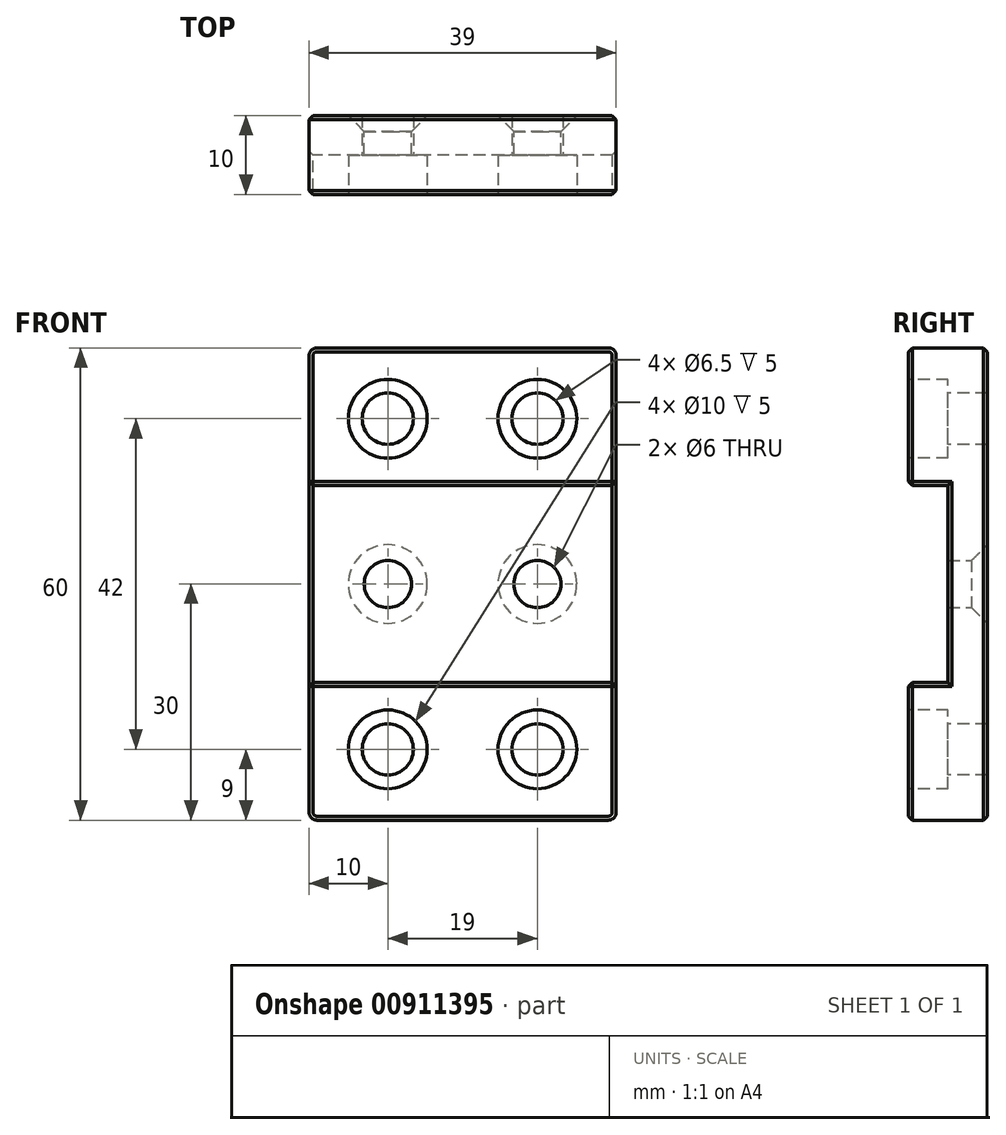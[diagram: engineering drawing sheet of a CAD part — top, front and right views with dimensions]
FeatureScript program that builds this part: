
annotation { "Feature Type Name" : "Feature", "Feature Type Description" : "" }
export const myFeature = defineFeature(function(context is Context, id is Id, definition is map)
    precondition{}
    {
        {
            var Q0;
            Q0=qCreatedBy(makeId("Right.planeOp"),FACE);
            var sketch = newSketch(context, id + "F0", { "sketchPlane" : qUnion([Q0])});
            skLineSegment(sketch, "E0", {"start": v(0, 0) * mm, "end": v(0, 60) * mm});
            skLineSegment(sketch, "E1", {"start": v(0, 60) * mm, "end": v(-10, 60) * mm});
            skLineSegment(sketch, "E2", {"start": v(-10, 60) * mm, "end": v(-10, 42.5) * mm});
            skLineSegment(sketch, "E3", {"start": v(-10, 42.5) * mm, "end": v(-5, 42.5) * mm});
            skLineSegment(sketch, "E4", {"start": v(-5, 42.5) * mm, "end": v(-5, 17.5) * mm});
            skLineSegment(sketch, "E5", {"start": v(-5, 17.5) * mm, "end": v(-10, 17.5) * mm});
            skLineSegment(sketch, "E6", {"start": v(-10, 17.5) * mm, "end": v(-10, 0) * mm});
            skLineSegment(sketch, "E7", {"start": v(-10, 0) * mm, "end": v(0, 0) * mm});
            skSolve(sketch);
        }
        {
            var Q0;
            Q0=makeQuery(id+"F0.imprint","IMPRINT",FACE,{"disambiguationData":[TD([[makeQuery(id+"F0.imprint","IMPRINT",EDGE,{"derivedFrom":sQuery(id+"F0.wireOp",EDGE,"E0")}),1.0]])]});
            extrude(context, id + "F1", {"entities" : qUnion([Q0]), "depth" : 39 * mm, "offsetDistance" : 25 * mm});
        }
        {
            var Q0;
            Q0=makeQuery(id+"F1.opExtrude","SWEPT_FACE",FACE,{"disambiguationData":[OSD([sQuery(id+"F0.wireOp",EDGE,"E2")])]});
            var sketch = newSketch(context, id + "F2", { "sketchPlane" : qUnion([Q0])});
            skCircle(sketch, "E8", {"center": v(10, 51) * mm, "radius": 3.25 * mm});
            skCircle(sketch, "E9.1.0.0", {"center": v(29, 51) * mm, "radius": 3.25 * mm});
            skLineSegment(sketch, "E9.direction1", {"start": v(10, 51) * mm, "end": v(29, 51) * mm, "construction": true});
            skSolve(sketch);
        }
        {
            var Q0;
            Q0=makeQuery(id+"F1.opExtrude","SWEPT_FACE",FACE,{"disambiguationData":[OSD([sQuery(id+"F0.wireOp",EDGE,"E6")])]});
            var sketch = newSketch(context, id + "F3", { "sketchPlane" : qUnion([Q0])});
            skCircle(sketch, "E10", {"center": v(10, 9) * mm, "radius": 3.25 * mm});
            skCircle(sketch, "E11.1.0.0", {"center": v(29, 9) * mm, "radius": 3.25 * mm});
            skLineSegment(sketch, "E11.direction1", {"start": v(10, 9) * mm, "end": v(29, 9) * mm, "construction": true});
            skSolve(sketch);
        }
        {
            var Q0;
            Q0=makeQuery(id+"F1.opExtrude","SWEPT_FACE",FACE,{"disambiguationData":[OSD([sQuery(id+"F0.wireOp",EDGE,"E0")])]});
            var sketch = newSketch(context, id + "F4", { "sketchPlane" : qUnion([Q0])});
            skCircle(sketch, "E12", {"center": v(-29, 30) * mm, "radius": 3 * mm});
            skCircle(sketch, "E13.1.0.0", {"center": v(-10, 30) * mm, "radius": 3 * mm});
            skLineSegment(sketch, "E13.direction1", {"start": v(-29, 30) * mm, "end": v(-10, 30) * mm, "construction": true});
            skSolve(sketch);
        }
        {
            var Q0;
            Q0=sQuery(id+"F4.wireOp",VERTEX,"E13.direction1.start");
            var Q1;
            Q1=sQuery(id+"F4.wireOp",VERTEX,"E13.direction1.end");
            var Q2;
            Q2=makeQuery(id+"F1.opExtrude","SWEPT_BODY",BODY,{"disambiguationData":[OSD([sQuery(id+"F0.wireOp",EDGE,"E0"),sQuery(id+"F0.wireOp",EDGE,"E1"),sQuery(id+"F0.wireOp",EDGE,"E2"),sQuery(id+"F0.wireOp",EDGE,"E3"),sQuery(id+"F0.wireOp",EDGE,"E4"),sQuery(id+"F0.wireOp",EDGE,"E5"),sQuery(id+"F0.wireOp",EDGE,"E6"),sQuery(id+"F0.wireOp",EDGE,"E7")])]});
            hole(context, id + "F5", {"style" : HoleStyle.C_SINK, "endStyle" : HoleEndStyle.THROUGH, "holeDiameter" : 6 * mm, "cSinkDiameter" : 10 * mm, "cSinkAngle" : 90 * degree, "majorDiameter" : 5 * mm, "isTappedThrough" : true, "tappedDepth" : 12 * mm, "tapClearance" : 3, "startFromSketch" : true, "locations" : qUnion([Q0, Q1]), "scope" : qUnion([Q2])});
        }
        {
            var Q0;
            Q0=sQuery(id+"F2.wireOp",VERTEX,"E9.direction1.start");
            var Q1;
            Q1=sQuery(id+"F2.wireOp",VERTEX,"E9.direction1.end");
            var Q2;
            Q2=sQuery(id+"F3.wireOp",VERTEX,"E11.direction1.start");
            var Q3;
            Q3=sQuery(id+"F3.wireOp",VERTEX,"E11.direction1.end");
            var Q4;
            Q4=makeQuery(id+"F1.opExtrude","SWEPT_BODY",BODY,{"disambiguationData":[OSD([sQuery(id+"F0.wireOp",EDGE,"E0"),sQuery(id+"F0.wireOp",EDGE,"E1"),sQuery(id+"F0.wireOp",EDGE,"E2"),sQuery(id+"F0.wireOp",EDGE,"E3"),sQuery(id+"F0.wireOp",EDGE,"E4"),sQuery(id+"F0.wireOp",EDGE,"E5"),sQuery(id+"F0.wireOp",EDGE,"E6"),sQuery(id+"F0.wireOp",EDGE,"E7")])]});
            hole(context, id + "F6", {"style" : HoleStyle.C_BORE, "endStyle" : HoleEndStyle.THROUGH, "holeDiameter" : 6.5 * mm, "cBoreDiameter" : 10 * mm, "cBoreDepth" : 5 * mm, "majorDiameter" : 5 * mm, "isTappedThrough" : true, "tappedDepth" : 12 * mm, "tapClearance" : 3, "startFromSketch" : true, "locations" : qUnion([Q0, Q1, Q2, Q3]), "scope" : qUnion([Q4])});
        }
        {
            var Q0;
            Q0=makeQuery(id+"F1.opExtrude","CAP_EDGE",EDGE,{"disambiguationData":[OSD([sQuery(id+"F0.wireOp",EDGE,"E1")])],"isStart":false});
            var Q1;
            Q1=makeQuery(id+"F1.opExtrude","CAP_EDGE",EDGE,{"disambiguationData":[OSD([sQuery(id+"F0.wireOp",EDGE,"E7")])],"isStart":false});
            var Q2;
            Q2=makeQuery(id+"F1.opExtrude","CAP_EDGE",EDGE,{"disambiguationData":[OSD([sQuery(id+"F0.wireOp",EDGE,"E1")])],"isStart":true});
            var Q3;
            Q3=makeQuery(id+"F1.opExtrude","CAP_EDGE",EDGE,{"disambiguationData":[OSD([sQuery(id+"F0.wireOp",EDGE,"E7")])],"isStart":true});
            fillet(context, id + "F7", {"entities" : qUnion([Q0, Q1, Q2, Q3]), "radius" : 1 * mm, "tangentPropagation" : true, "allowEdgeOverflow" : false});
        }
        {
            var Q0;
            Q0=makeQuery(id+"F1.opExtrude","SWEPT_EDGE",EDGE,{"disambiguationData":[OSD([sQuery(id+"F0.wireOp",EDGE,"E2"),sQuery(id+"F0.wireOp",EDGE,"E3")])]});
            var Q1;
            Q1=makeQuery(id+"F1.opExtrude","SWEPT_EDGE",EDGE,{"disambiguationData":[OSD([sQuery(id+"F0.wireOp",EDGE,"E5"),sQuery(id+"F0.wireOp",EDGE,"E6")])]});
            var Q2;
            Q2=makeQuery(id+"F1.opExtrude","CAP_EDGE",EDGE,{"disambiguationData":[OSD([sQuery(id+"F0.wireOp",EDGE,"E3")])],"isStart":false});
            var Q3;
            Q3=makeQuery(id+"F1.opExtrude","CAP_EDGE",EDGE,{"disambiguationData":[OSD([sQuery(id+"F0.wireOp",EDGE,"E4")])],"isStart":false});
            var Q4;
            Q4=makeQuery(id+"F1.opExtrude","CAP_EDGE",EDGE,{"disambiguationData":[OSD([sQuery(id+"F0.wireOp",EDGE,"E5")])],"isStart":false});
            var Q5;
            Q5=makeQuery(id+"F1.opExtrude","CAP_EDGE",EDGE,{"disambiguationData":[OSD([sQuery(id+"F0.wireOp",EDGE,"E2")])],"isStart":false});
            var Q6;
            Q6=makeQuery(id+"F1.opExtrude","CAP_EDGE",EDGE,{"disambiguationData":[OSD([sQuery(id+"F0.wireOp",EDGE,"E6")])],"isStart":false});
            var Q7;
            Q7=makeQuery(id+"F1.opExtrude","CAP_EDGE",EDGE,{"disambiguationData":[OSD([sQuery(id+"F0.wireOp",EDGE,"E3")])],"isStart":true});
            var Q8;
            Q8=makeQuery(id+"F1.opExtrude","CAP_EDGE",EDGE,{"disambiguationData":[OSD([sQuery(id+"F0.wireOp",EDGE,"E5")])],"isStart":true});
            var Q9;
            Q9=makeQuery(id+"F1.opExtrude","CAP_EDGE",EDGE,{"disambiguationData":[OSD([sQuery(id+"F0.wireOp",EDGE,"E2")])],"isStart":true});
            var Q10;
            Q10=makeQuery(id+"F1.opExtrude","CAP_EDGE",EDGE,{"disambiguationData":[OSD([sQuery(id+"F0.wireOp",EDGE,"E0")])],"isStart":true});
            var Q11;
            Q11=makeQuery(id+"F1.opExtrude","CAP_EDGE",EDGE,{"disambiguationData":[OSD([sQuery(id+"F0.wireOp",EDGE,"E4")])],"isStart":true});
            chamfer(context, id + "F8", {"entities" : qUnion([Q0, Q1, Q2, Q3, Q4, Q5, Q6, Q7, Q8, Q9, Q10, Q11]), "width" : 0.5 * mm, "tangentPropagation" : true});
        }
    });
